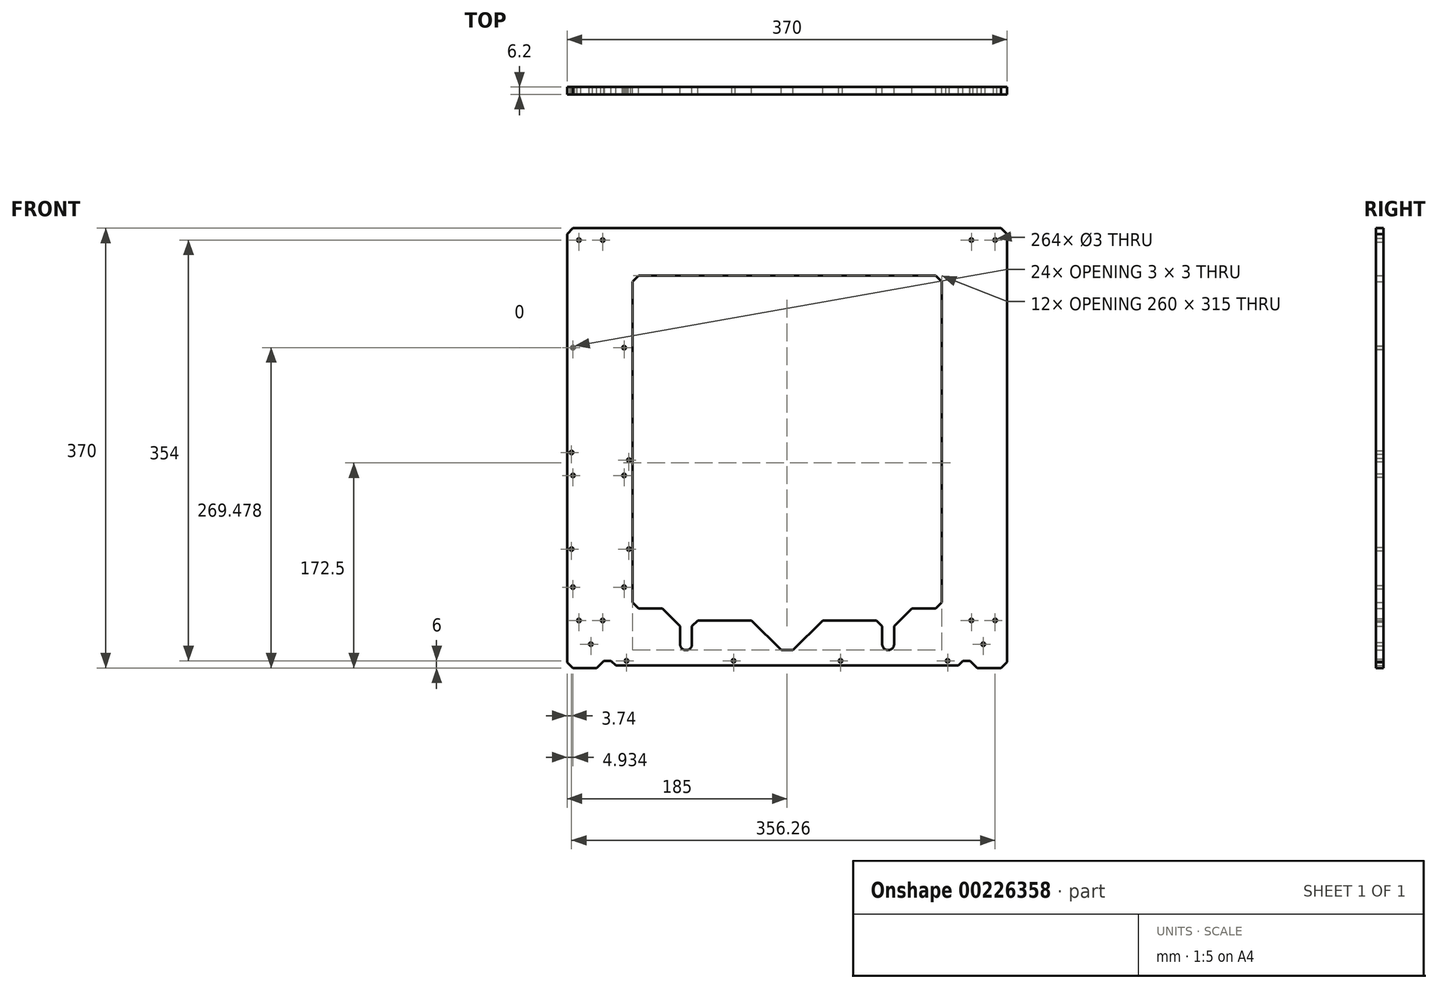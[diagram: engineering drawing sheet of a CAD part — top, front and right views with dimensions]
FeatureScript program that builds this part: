
annotation { "Feature Type Name" : "Feature", "Feature Type Description" : "" }
export const myFeature = defineFeature(function(context is Context, id is Id, definition is map)
    precondition{}
    {
        {
            var Q0;
            Q0=qCreatedBy(makeId("Front.planeOp"),FACE);
            var sketch = newSketch(context, id + "F0", { "sketchPlane" : qUnion([Q0])});
            skLineSegment(sketch, "E0", {"start": v(-180, -185) * mm, "end": v(-185, -180.2) * mm});
            skLineSegment(sketch, "E1", {"start": v(-185, -180.2) * mm, "end": v(-185, 180) * mm});
            skLineSegment(sketch, "E2", {"start": v(-185, 180) * mm, "end": v(-180, 185) * mm});
            skLineSegment(sketch, "E3", {"start": v(-180, 185) * mm, "end": v(180, 185) * mm});
            skLineSegment(sketch, "E4", {"start": v(180, 185) * mm, "end": v(185, 180) * mm});
            skLineSegment(sketch, "E5", {"start": v(185, 180) * mm, "end": v(185, -180) * mm});
            skLineSegment(sketch, "E6", {"start": v(185, -180) * mm, "end": v(180, -185) * mm});
            skLineSegment(sketch, "E7", {"start": v(180, -185) * mm, "end": v(160, -185) * mm});
            skLineSegment(sketch, "E8", {"start": v(160, -185) * mm, "end": v(158, -183) * mm});
            skLineSegment(sketch, "E9", {"start": v(144, -183) * mm, "end": v(-144, -183) * mm});
            skLineSegment(sketch, "E10", {"start": v(-158, -183) * mm, "end": v(-160, -185) * mm});
            skLineSegment(sketch, "E11", {"start": v(-160, -185) * mm, "end": v(-180, -185) * mm});
            skArc(sketch, "E12", {"start": v(-90, -165) * mm, "mid": v(-85, -170) * mm, "end": v(-80, -165) * mm});
            skLineSegment(sketch, "E13", {"start": v(-90, -165) * mm, "end": v(-90, -150) * mm});
            skLineSegment(sketch, "E14", {"start": v(-90, -150) * mm, "end": v(-105, -135) * mm});
            skLineSegment(sketch, "E15", {"start": v(-105, -135) * mm, "end": v(-125, -135) * mm});
            skLineSegment(sketch, "E16", {"start": v(-125, -135) * mm, "end": v(-130, -130) * mm});
            skLineSegment(sketch, "E17", {"start": v(-130, -130) * mm, "end": v(-130, 140) * mm});
            skLineSegment(sketch, "E18", {"start": v(-130, 140) * mm, "end": v(-125, 145) * mm});
            skLineSegment(sketch, "E19", {"start": v(-125, 145) * mm, "end": v(125, 145) * mm});
            skLineSegment(sketch, "E20", {"start": v(125, 145) * mm, "end": v(130, 140) * mm});
            skLineSegment(sketch, "E21", {"start": v(130, 140) * mm, "end": v(130, -130) * mm});
            skLineSegment(sketch, "E22", {"start": v(130, -130) * mm, "end": v(125, -135) * mm});
            skLineSegment(sketch, "E23", {"start": v(-80, -165) * mm, "end": v(-80, -150) * mm});
            skLineSegment(sketch, "E24", {"start": v(-80, -150) * mm, "end": v(-75, -145) * mm});
            skArc(sketch, "E25", {"start": v(80, -165) * mm, "mid": v(85, -170) * mm, "end": v(90, -165) * mm});
            skLineSegment(sketch, "E26", {"start": v(125, -135) * mm, "end": v(105, -135) * mm});
            skLineSegment(sketch, "E27", {"start": v(105, -135) * mm, "end": v(90, -150) * mm});
            skLineSegment(sketch, "E28", {"start": v(90, -150) * mm, "end": v(90, -165) * mm});
            skLineSegment(sketch, "E29", {"start": v(80, -165) * mm, "end": v(80, -150) * mm});
            skLineSegment(sketch, "E30", {"start": v(80, -150) * mm, "end": v(75, -145) * mm});
            skLineSegment(sketch, "E31", {"start": v(-5, -170) * mm, "end": v(5, -170) * mm});
            skLineSegment(sketch, "E32", {"start": v(5, -170) * mm, "end": v(30, -145) * mm});
            skLineSegment(sketch, "E33", {"start": v(-5, -170) * mm, "end": v(-30, -145) * mm});
            skLineSegment(sketch, "E34", {"start": v(-75, -145) * mm, "end": v(-30, -145) * mm});
            skLineSegment(sketch, "E35", {"start": v(30, -145) * mm, "end": v(75, -145) * mm});
            skCircle(sketch, "E36", {"center": v(-181.26, -3.72) * mm, "radius": 1.5 * mm});
            skCircle(sketch, "E37", {"center": v(-133, -10.07) * mm, "radius": 1.5 * mm});
            skCircle(sketch, "E38", {"center": v(-133, -85) * mm, "radius": 1.5 * mm});
            skCircle(sketch, "E39", {"center": v(-181.26, -85) * mm, "radius": 1.5 * mm});
            skLineSegment(sketch, "E40", {"start": v(158, -183) * mm, "end": v(154, -179) * mm});
            skLineSegment(sketch, "E41", {"start": v(154, -179) * mm, "end": v(148, -179) * mm});
            skLineSegment(sketch, "E42", {"start": v(148, -179) * mm, "end": v(144, -183) * mm});
            skLineSegment(sketch, "E43", {"start": v(-158, -183) * mm, "end": v(-154, -179) * mm});
            skLineSegment(sketch, "E44", {"start": v(-154, -179) * mm, "end": v(-148, -179) * mm});
            skLineSegment(sketch, "E45", {"start": v(-148, -179) * mm, "end": v(-144, -183) * mm});
            skCircle(sketch, "E46", {"center": v(-135, -179) * mm, "radius": 1.5 * mm});
            skCircle(sketch, "E47", {"center": v(135, -179) * mm, "radius": 1.5 * mm});
            skCircle(sketch, "E48", {"center": v(45, -179) * mm, "radius": 1.5 * mm});
            skCircle(sketch, "E49", {"center": v(-45, -179) * mm, "radius": 1.5 * mm});
            skCircle(sketch, "E50", {"center": v(-175, -145) * mm, "radius": 1.5 * mm});
            skCircle(sketch, "E51", {"center": v(-155, -145) * mm, "radius": 1.5 * mm});
            skCircle(sketch, "E52", {"center": v(-165, -165) * mm, "radius": 1.5 * mm});
            skCircle(sketch, "E53", {"center": v(165, -165) * mm, "radius": 1.5 * mm});
            skCircle(sketch, "E54", {"center": v(155, -145) * mm, "radius": 1.5 * mm});
            skCircle(sketch, "E55", {"center": v(175, -145) * mm, "radius": 1.5 * mm});
            skCircle(sketch, "E56", {"center": v(175, 175) * mm, "radius": 1.5 * mm});
            skCircle(sketch, "E57", {"center": v(155, 175) * mm, "radius": 1.5 * mm});
            skCircle(sketch, "E58", {"center": v(-175, 175) * mm, "radius": 1.5 * mm});
            skCircle(sketch, "E59", {"center": v(-155, 175) * mm, "radius": 1.5 * mm});
            skCircle(sketch, "E60", {"center": v(-137.05, -117.03) * mm, "radius": 1.5 * mm});
            skCircle(sketch, "E61", {"center": v(-180.05, -23.03) * mm, "radius": 1.5 * mm});
            skCircle(sketch, "E62", {"center": v(-137.05, -23.03) * mm, "radius": 1.5 * mm});
            skCircle(sketch, "E63", {"center": v(-180.05, 84.47) * mm, "radius": 1.5 * mm});
            skCircle(sketch, "E64", {"center": v(-137.05, 84.47) * mm, "radius": 1.5 * mm});
            skCircle(sketch, "E65", {"center": v(-180.08, -117) * mm, "radius": 1.5 * mm});
            skCircle(sketch, "E66", {"center": v(-180.08, 84.5) * mm, "radius": 1.5 * mm});
            skCircle(sketch, "E67", {"center": v(-137.08, 84.5) * mm, "radius": 1.5 * mm});
            skLineSegment(sketch, "E68", {"start": v(0, 185) * mm, "end": v(0, -183) * mm, "construction": true});
            skLineSegment(sketch, "E69", {"start": v(185, 0) * mm, "end": v(-185, 0) * mm, "construction": true});
            skSolve(sketch);
        }
        {
            var Q0;
            Q0 = qSketchRegion(id + "F0", true);
            extrude(context, id + "F1", {"entities" : qUnion([Q0]), "depth" : 6.2 * mm});
        }
    });
